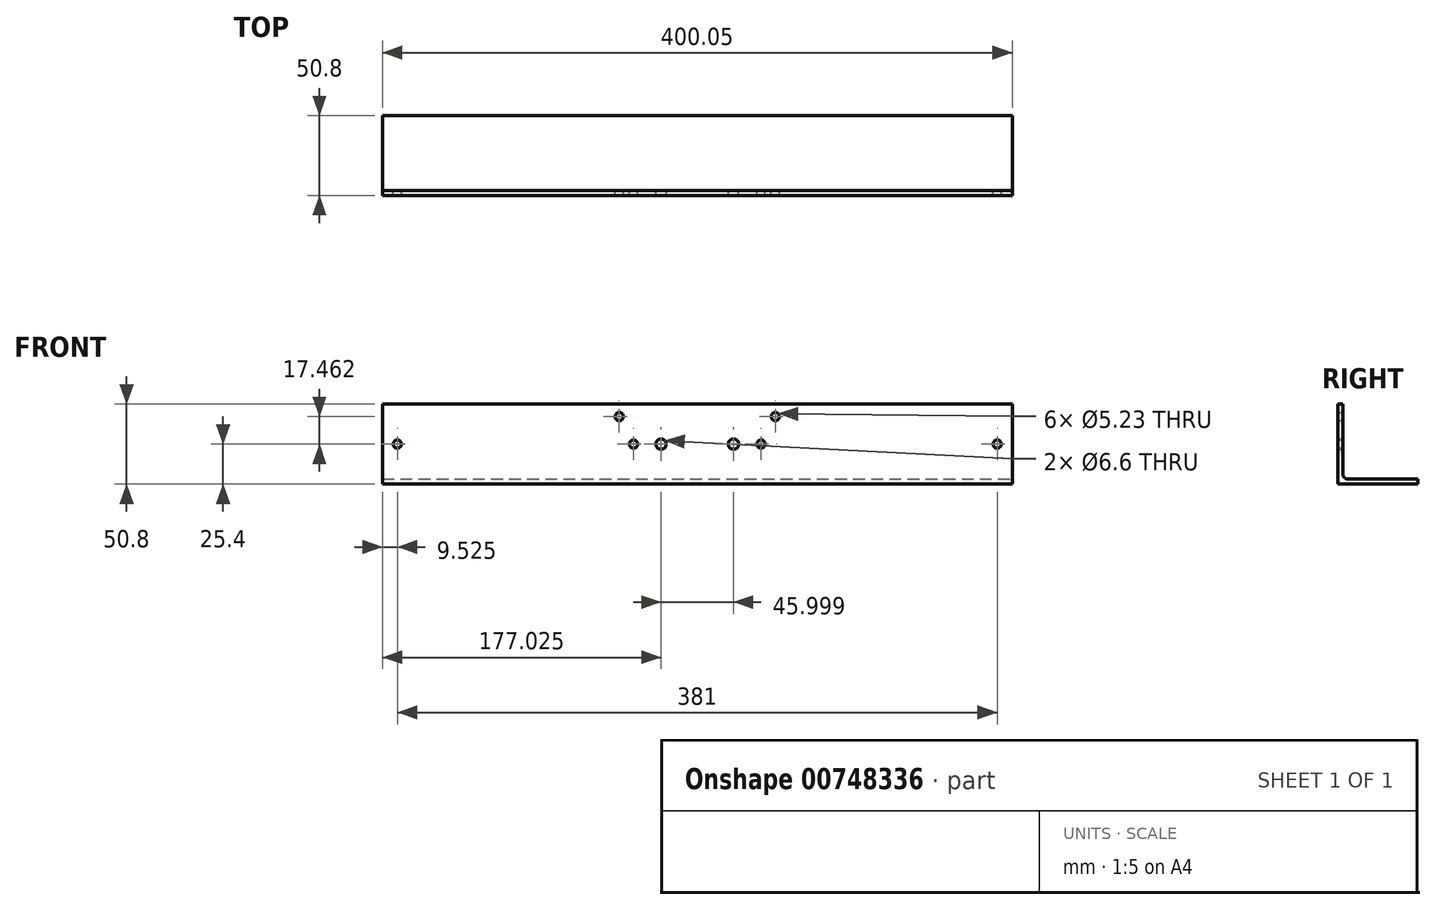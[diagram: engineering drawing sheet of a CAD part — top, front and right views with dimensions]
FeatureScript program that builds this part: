
annotation { "Feature Type Name" : "Feature", "Feature Type Description" : "" }
export const myFeature = defineFeature(function(context is Context, id is Id, definition is map)
    precondition{}
    {
        {
            var Q0;
            Q0=qCreatedBy(makeId("Right.planeOp"),FACE);
            var sketch = newSketch(context, id + "F0", { "sketchPlane" : qUnion([Q0])});
            skLineSegment(sketch, "E0", {"start": v(0, 0) * mm, "end": v(0, -44.45) * mm});
            skLineSegment(sketch, "E1", {"start": v(3.18, -47.63) * mm, "end": v(47.63, -47.62) * mm});
            skLineSegment(sketch, "E2.0", {"start": v(-3.17, -50.8) * mm, "end": v(47.63, -50.8) * mm});
            skLineSegment(sketch, "E2.1", {"start": v(-3.18, 0) * mm, "end": v(-3.17, -50.8) * mm});
            skLineSegment(sketch, "E3", {"start": v(-3.18, 0) * mm, "end": v(0, 0) * mm});
            skLineSegment(sketch, "E4", {"start": v(47.63, -47.62) * mm, "end": v(47.63, -50.8) * mm});
            skPoint(sketch, "E5.visualSharp", {"position": v(0, -47.63) * mm});
            skArc(sketch, "E5.filletArc", {"start": v(0, -44.45) * mm, "mid": v(0.93, -46.7) * mm, "end": v(3.18, -47.63) * mm});
            skSolve(sketch);
        }
        {
            var Q0;
            Q0=makeQuery(id+"F0.imprint","IMPRINT",FACE,{"disambiguationData":[TD([[makeQuery(id+"F0.imprint","IMPRINT",EDGE,{"derivedFrom":sQuery(id+"F0.wireOp",EDGE,"E0")}),-1.0]])]});
            extrude(context, id + "F1", {"entities" : qUnion([Q0]), "oppositeDirection" : true, "depth" : 400.05 * mm, "offsetDistance" : 25.4 * mm});
        }
        {
            var Q0;
            Q0=makeQuery(id+"F1.opExtrude","SWEPT_FACE",FACE,{"disambiguationData":[OSD([sQuery(id+"F0.wireOp",EDGE,"E0")])]});
            var sketch = newSketch(context, id + "F2", { "sketchPlane" : qUnion([Q0])});
            skLineSegment(sketch, "E6.right", {"start": v(9.53, 0) * mm, "end": v(9.53, -50.8) * mm, "construction": true});
            skLineSegment(sketch, "E7.right", {"start": v(390.53, 0) * mm, "end": v(390.53, -25.4) * mm, "construction": true});
            skLineSegment(sketch, "E8.left", {"start": v(9.53, 0) * mm, "end": v(9.53, -25.4) * mm, "construction": true});
            skLineSegment(sketch, "E9.right", {"start": v(390.53, -25.4) * mm, "end": v(390.53, -25.4) * mm});
            skCircle(sketch, "E10", {"center": v(9.53, -25.4) * mm, "radius": 2.62 * mm});
            skCircle(sketch, "E11", {"center": v(390.53, -25.4) * mm, "radius": 2.62 * mm});
            skLineSegment(sketch, "E12", {"start": v(9.53, -25.4) * mm, "end": v(390.53, -25.4) * mm, "construction": true});
            skLineSegment(sketch, "E13", {"start": v(200.03, 0) * mm, "end": v(200.03, -44.45) * mm, "construction": true});
            skLineSegment(sketch, "E14.0", {"start": v(240.51, 0) * mm, "end": v(240.51, -44.45) * mm, "construction": true});
            skLineSegment(sketch, "E15.0", {"start": v(159.54, 0) * mm, "end": v(159.54, -44.45) * mm, "construction": true});
            skCircle(sketch, "E16", {"center": v(159.54, -25.4) * mm, "radius": 2.62 * mm});
            skCircle(sketch, "E17", {"center": v(240.51, -25.4) * mm, "radius": 2.62 * mm});
            skLineSegment(sketch, "E18.bottom", {"start": v(223.02, -31.9) * mm, "end": v(177.03, -31.9) * mm, "construction": true});
            skLineSegment(sketch, "E18.top", {"start": v(223.02, -18.9) * mm, "end": v(177.03, -18.9) * mm, "construction": true});
            skLineSegment(sketch, "E18.left", {"start": v(223.02, -31.9) * mm, "end": v(223.02, -18.9) * mm, "construction": true});
            skLineSegment(sketch, "E18.right", {"start": v(177.03, -31.9) * mm, "end": v(177.03, -18.9) * mm, "construction": true});
            skPoint(sketch, "E18.middle", {"position": v(200.03, -25.4) * mm});
            skCircle(sketch, "E19", {"center": v(223.02, -25.4) * mm, "radius": 3.3 * mm});
            skCircle(sketch, "E20", {"center": v(177.03, -25.4) * mm, "radius": 3.3 * mm});
            skLineSegment(sketch, "E21", {"start": v(400.05, -7.94) * mm, "end": v(0, -7.94) * mm, "construction": true});
            skCircle(sketch, "E22", {"center": v(249.6, -7.94) * mm, "radius": 2.62 * mm});
            skCircle(sketch, "E23", {"center": v(150.47, -7.94) * mm, "radius": 2.62 * mm});
            skSolve(sketch);
        }
        {
            var Q0;
            Q0=qSketchRegion(id+"F2",true);
            extrude(context, id + "F3", {"entities" : qUnion([Q0]), "operationType" : NewBodyOperationType.REMOVE, "endBound" : BoundingType.THROUGH_ALL, "oppositeDirection" : true, "depth" : 25.4 * mm, "offsetDistance" : 25.4 * mm});
        }
    });
